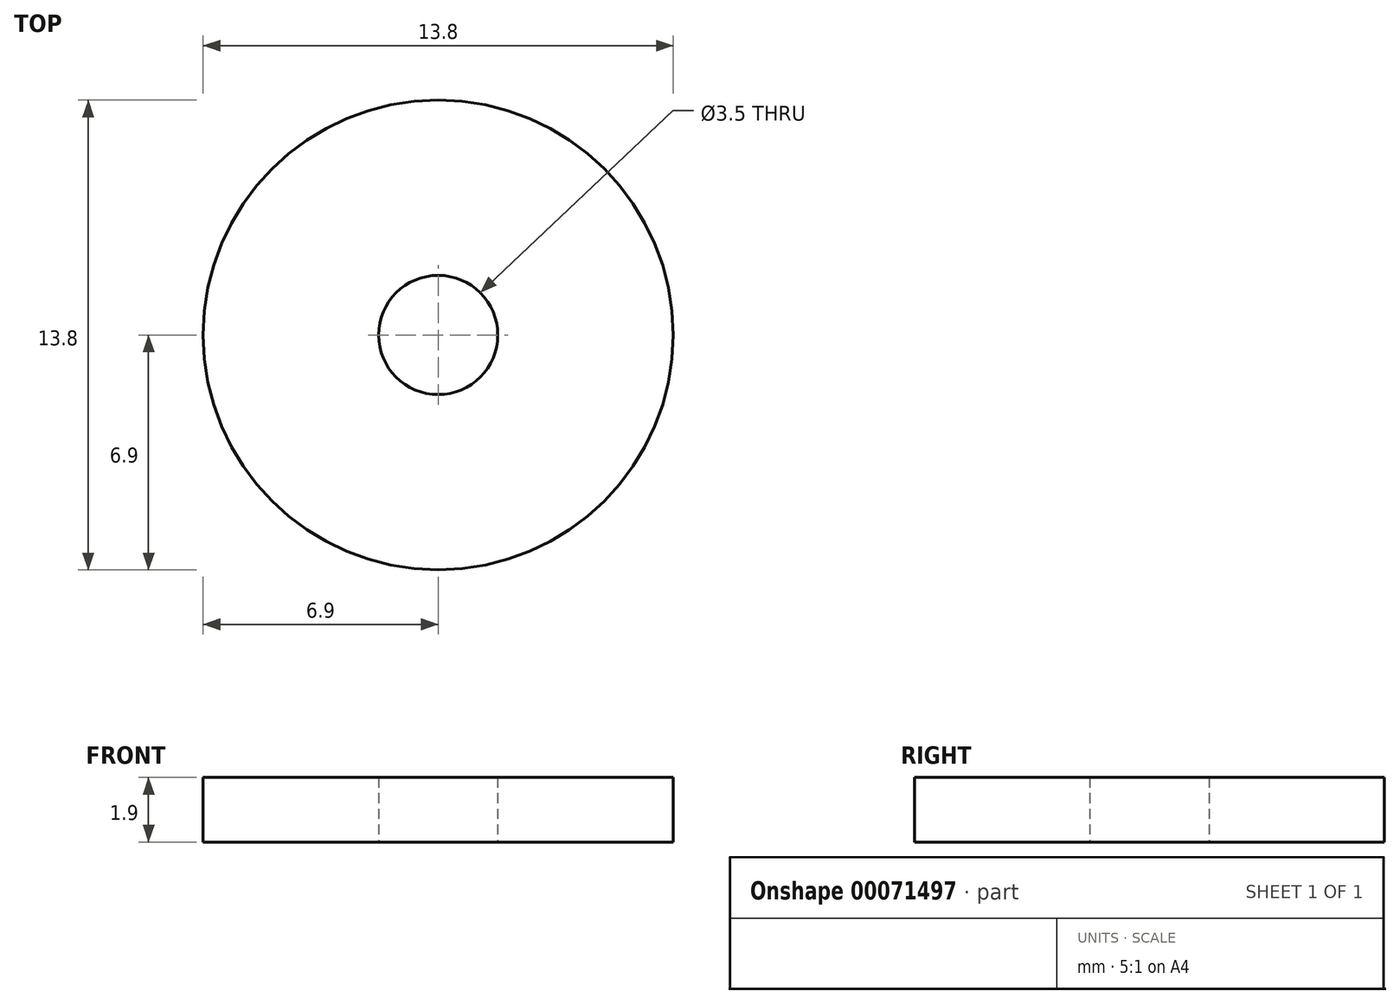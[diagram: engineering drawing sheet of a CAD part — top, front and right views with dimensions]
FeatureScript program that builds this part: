
annotation { "Feature Type Name" : "Feature", "Feature Type Description" : "" }
export const myFeature = defineFeature(function(context is Context, id is Id, definition is map)
    precondition{}
    {
        {
            var Q0;
            Q0=qCreatedBy(makeId("Top.planeOp"),FACE);
            var sketch = newSketch(context, id + "F0", { "sketchPlane" : qUnion([Q0])});
            skCircle(sketch, "E0", {"center": v(0, 0) * mm, "radius": 1.75 * mm});
            skCircle(sketch, "E1", {"center": v(0, 0) * mm, "radius": 6.9 * mm});
            skSolve(sketch);
        }
        {
            var Q0;
            Q0=makeQuery(id+"F0.imprint","IMPRINT",FACE,{"disambiguationData":[TD([[makeQuery(id+"F0.imprint","IMPRINT",EDGE,{"derivedFrom":sQuery(id+"F0.wireOp",EDGE,"E0")}),-1.0]])]});
            extrude(context, id + "F1", {"entities" : qUnion([Q0]), "depth" : 1.9 * mm});
        }
    });
